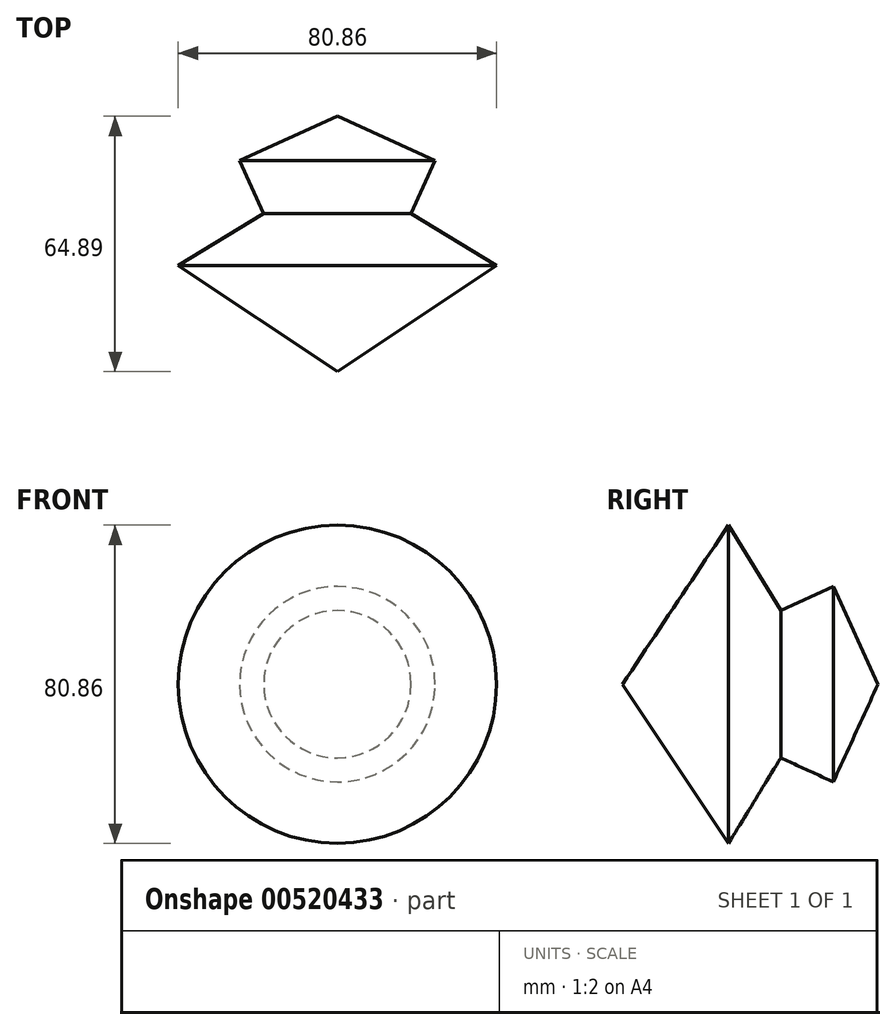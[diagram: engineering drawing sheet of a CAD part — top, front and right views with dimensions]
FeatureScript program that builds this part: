
annotation { "Feature Type Name" : "Feature", "Feature Type Description" : "" }
export const myFeature = defineFeature(function(context is Context, id is Id, definition is map)
    precondition{}
    {
        {
            var Q0;
            Q0=qCreatedBy(makeId("Top.planeOp"),FACE);
            var sketch = newSketch(context, id + "F0", { "sketchPlane" : qUnion([Q0])});
            skLineSegment(sketch, "E0", {"start": v(0, 0) * mm, "end": v(0, 64.9) * mm});
            skLineSegment(sketch, "E1", {"start": v(0, 64.9) * mm, "end": v(-24.82, 53.55) * mm});
            skLineSegment(sketch, "E2", {"start": v(-24.82, 53.55) * mm, "end": v(-18.72, 40.2) * mm});
            skLineSegment(sketch, "E3", {"start": v(-18.72, 40.2) * mm, "end": v(-40.43, 26.95) * mm});
            skLineSegment(sketch, "E4", {"start": v(-40.43, 26.95) * mm, "end": v(0, 0) * mm});
            skSolve(sketch);
        }
        {
            var Q0;
            Q0=makeQuery(id+"F0.imprint","IMPRINT",FACE,{"disambiguationData":[TD([[makeQuery(id+"F0.imprint","IMPRINT",EDGE,{"derivedFrom":sQuery(id+"F0.wireOp",EDGE,"E0")}),1.0]])]});
            var Q1;
            Q1=sQuery(id+"F0.wireOp",EDGE,"E0");
            revolve(context, id + "F1", {"entities" : qUnion([Q0]), "axis" : qUnion([Q1]), "revolveType" : RevolveType.FULL});
        }
    });
